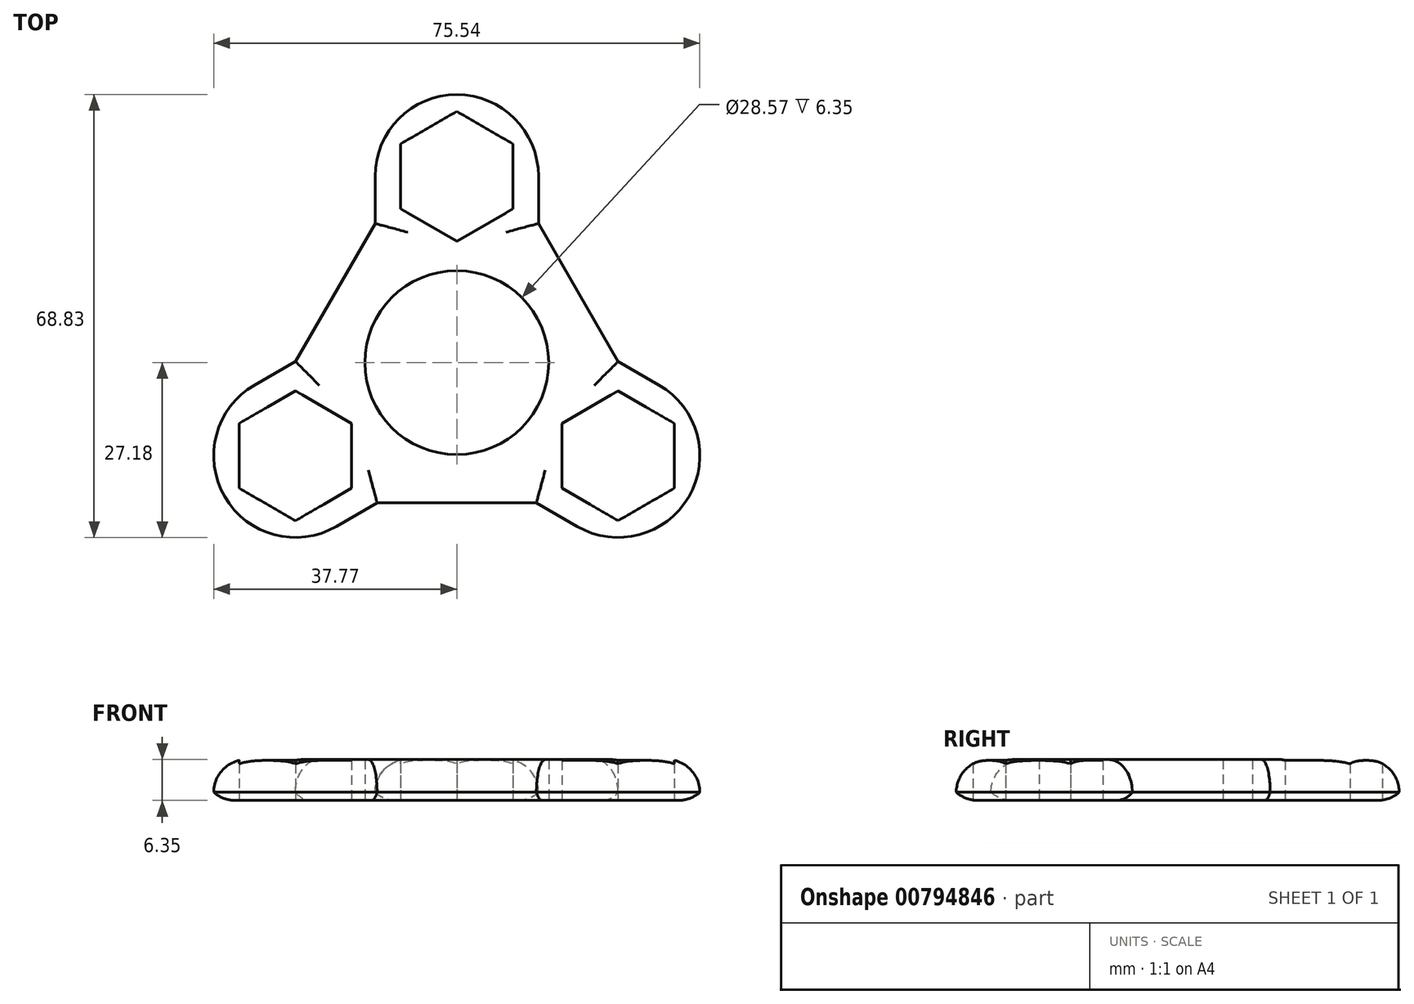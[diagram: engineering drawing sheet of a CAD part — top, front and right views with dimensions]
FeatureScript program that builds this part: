
annotation { "Feature Type Name" : "Feature", "Feature Type Description" : "" }
export const myFeature = defineFeature(function(context is Context, id is Id, definition is map)
    precondition{}
    {
        {
            var Q0;
            Q0=qCreatedBy(makeId("Top.planeOp"),FACE);
            var sketch = newSketch(context, id + "F0", { "sketchPlane" : qUnion([Q0])});
            skCircle(sketch, "E0", {"center": v(0, 0) * mm, "radius": 11.02 * mm});
            skCircle(sketch, "E1", {"center": v(0, 0) * mm, "radius": 14.29 * mm});
            skCircle(sketch, "E2.cCircle", {"center": v(0, 28.95) * mm, "radius": 8.74 * mm, "construction": true});
            skLineSegment(sketch, "E2.0", {"start": v(-8.74, 23.9) * mm, "end": v(-8.74, 34) * mm});
            skLineSegment(sketch, "E2.1", {"start": v(-8.74, 34) * mm, "end": v(0, 39.04) * mm});
            skLineSegment(sketch, "E2.2", {"start": v(0, 39.04) * mm, "end": v(8.74, 34) * mm});
            skLineSegment(sketch, "E2.3", {"start": v(8.74, 34) * mm, "end": v(8.74, 23.9) * mm});
            skLineSegment(sketch, "E2.4", {"start": v(8.74, 23.9) * mm, "end": v(0, 18.86) * mm});
            skLineSegment(sketch, "E2.5", {"start": v(0, 18.86) * mm, "end": v(-8.74, 23.9) * mm});
            skPoint(sketch, "E2.0.midPoint", {"position": v(-8.74, 28.95) * mm});
            skCircle(sketch, "E3.cCircle", {"center": v(0, 28.95) * mm, "radius": 12.7 * mm, "construction": true});
            skLineSegment(sketch, "E3.0", {"start": v(-12.7, 21.62) * mm, "end": v(-12.7, 36.28) * mm});
            skLineSegment(sketch, "E3.1", {"start": v(-12.7, 36.28) * mm, "end": v(0, 43.62) * mm});
            skLineSegment(sketch, "E3.2", {"start": v(0, 43.62) * mm, "end": v(12.7, 36.28) * mm});
            skLineSegment(sketch, "E3.3", {"start": v(12.7, 36.28) * mm, "end": v(12.7, 21.62) * mm});
            skLineSegment(sketch, "E3.4", {"start": v(12.7, 21.62) * mm, "end": v(0, 14.29) * mm});
            skLineSegment(sketch, "E3.5", {"start": v(0, 14.29) * mm, "end": v(-12.7, 21.62) * mm});
            skPoint(sketch, "E3.0.midPoint", {"position": v(-12.7, 28.95) * mm});
            skLineSegment(sketch, "E4.1.0", {"start": v(-25.07, -4.39) * mm, "end": v(-16.34, -9.43) * mm});
            skLineSegment(sketch, "E4.1.1", {"start": v(-33.81, -9.43) * mm, "end": v(-25.07, -4.39) * mm});
            skLineSegment(sketch, "E4.1.2", {"start": v(-16.34, -9.43) * mm, "end": v(-16.34, -19.52) * mm});
            skCircle(sketch, "E4.1.3", {"center": v(-25.07, -14.48) * mm, "radius": 12.7 * mm, "construction": true});
            skLineSegment(sketch, "E4.1.4", {"start": v(-12.37, -7.14) * mm, "end": v(-12.37, -21.8) * mm});
            skLineSegment(sketch, "E4.1.5", {"start": v(-12.37, -21.8) * mm, "end": v(-25.07, -29.14) * mm});
            skLineSegment(sketch, "E4.1.6", {"start": v(-25.07, -29.14) * mm, "end": v(-37.77, -21.8) * mm});
            skLineSegment(sketch, "E4.1.7", {"start": v(-25.07, 0.19) * mm, "end": v(-12.37, -7.14) * mm});
            skLineSegment(sketch, "E4.1.8", {"start": v(-37.77, -21.8) * mm, "end": v(-37.77, -7.14) * mm});
            skPoint(sketch, "E4.1.9", {"position": v(-20.7, -22.04) * mm});
            skLineSegment(sketch, "E4.1.10", {"start": v(-33.81, -19.52) * mm, "end": v(-33.81, -9.43) * mm});
            skPoint(sketch, "E4.1.11", {"position": v(-18.72, -25.47) * mm});
            skCircle(sketch, "E4.1.12", {"center": v(-25.07, -14.48) * mm, "radius": 8.74 * mm, "construction": true});
            skLineSegment(sketch, "E4.1.13", {"start": v(-37.77, -7.14) * mm, "end": v(-25.07, 0.19) * mm});
            skLineSegment(sketch, "E4.1.14", {"start": v(-16.34, -19.52) * mm, "end": v(-25.07, -24.57) * mm});
            skLineSegment(sketch, "E4.1.15", {"start": v(-25.07, -24.57) * mm, "end": v(-33.81, -19.52) * mm});
            skLineSegment(sketch, "E4.2.0", {"start": v(16.34, -19.52) * mm, "end": v(16.34, -9.43) * mm});
            skLineSegment(sketch, "E4.2.1", {"start": v(25.07, -24.57) * mm, "end": v(16.34, -19.52) * mm});
            skLineSegment(sketch, "E4.2.2", {"start": v(16.34, -9.43) * mm, "end": v(25.07, -4.39) * mm});
            skCircle(sketch, "E4.2.3", {"center": v(25.07, -14.48) * mm, "radius": 12.7 * mm, "construction": true});
            skLineSegment(sketch, "E4.2.4", {"start": v(12.37, -7.14) * mm, "end": v(25.07, 0.19) * mm});
            skLineSegment(sketch, "E4.2.5", {"start": v(25.07, 0.19) * mm, "end": v(37.77, -7.14) * mm});
            skLineSegment(sketch, "E4.2.6", {"start": v(37.77, -7.14) * mm, "end": v(37.77, -21.8) * mm});
            skLineSegment(sketch, "E4.2.7", {"start": v(12.37, -21.8) * mm, "end": v(12.37, -7.14) * mm});
            skLineSegment(sketch, "E4.2.8", {"start": v(37.77, -21.8) * mm, "end": v(25.07, -29.14) * mm});
            skPoint(sketch, "E4.2.9", {"position": v(29.44, -6.9) * mm});
            skLineSegment(sketch, "E4.2.10", {"start": v(33.81, -19.52) * mm, "end": v(25.07, -24.57) * mm});
            skPoint(sketch, "E4.2.11", {"position": v(31.42, -3.48) * mm});
            skCircle(sketch, "E4.2.12", {"center": v(25.07, -14.48) * mm, "radius": 8.74 * mm, "construction": true});
            skLineSegment(sketch, "E4.2.13", {"start": v(25.07, -29.14) * mm, "end": v(12.37, -21.8) * mm});
            skLineSegment(sketch, "E4.2.14", {"start": v(25.07, -4.39) * mm, "end": v(33.81, -9.43) * mm});
            skLineSegment(sketch, "E4.2.15", {"start": v(33.81, -9.43) * mm, "end": v(33.81, -19.52) * mm});
            skLineSegment(sketch, "E5", {"start": v(-12.7, 21.62) * mm, "end": v(-25.07, 0.19) * mm});
            skLineSegment(sketch, "E6", {"start": v(12.7, 21.62) * mm, "end": v(25.07, 0.19) * mm});
            skLineSegment(sketch, "E7", {"start": v(-12.37, -21.8) * mm, "end": v(12.37, -21.8) * mm});
            skArc(sketch, "E8", {"start": v(12.7, 28.95) * mm, "mid": v(0, 41.65) * mm, "end": v(-12.7, 28.95) * mm});
            skLineSegment(sketch, "E9", {"start": v(-12.7, 28.95) * mm, "end": v(-12.7, 36.28) * mm});
            skLineSegment(sketch, "E10", {"start": v(-12.7, 28.95) * mm, "end": v(-12.7, 36.28) * mm, "construction": true});
            skLineSegment(sketch, "E11", {"start": v(-12.7, 36.28) * mm, "end": v(0, 43.62) * mm, "construction": true});
            skLineSegment(sketch, "E12", {"start": v(0, 43.62) * mm, "end": v(12.7, 36.28) * mm, "construction": true});
            skLineSegment(sketch, "E13", {"start": v(12.7, 36.28) * mm, "end": v(12.7, 28.95) * mm, "construction": true});
            skSolve(sketch);
        }
        {
            var Q0;
            Q0 = qSketchRegion(id + "F0", true);
            extrude(context, id + "F1", {"entities" : qUnion([Q0]), "depth" : 6.35 * mm, "offsetDistance" : 25.4 * mm});
        }
        {
            var Q0;
            Q0=qCreatedBy(makeId("Top.planeOp"),FACE);
            var sketch = newSketch(context, id + "F2", { "sketchPlane" : qUnion([Q0])});
            skArc(sketch, "E14", {"start": v(12.7, 28.95) * mm, "mid": v(0, 41.65) * mm, "end": v(-12.7, 28.95) * mm});
            skLineSegment(sketch, "E15", {"start": v(-12.7, 28.95) * mm, "end": v(-12.7, 36.28) * mm});
            skLineSegment(sketch, "E16", {"start": v(-12.7, 36.28) * mm, "end": v(0, 43.62) * mm});
            skLineSegment(sketch, "E17", {"start": v(0, 43.62) * mm, "end": v(12.7, 36.28) * mm});
            skLineSegment(sketch, "E18", {"start": v(12.7, 36.28) * mm, "end": v(12.7, 28.95) * mm});
            skSolve(sketch);
        }
        {
            var Q0;
            Q0 = qSketchRegion(id + "F2", true);
            extrude(context, id + "F3", {"entities" : qUnion([Q0]), "operationType" : NewBodyOperationType.REMOVE, "endBound" : BoundingType.THROUGH_ALL, "depth" : 25.4 * mm, "offsetDistance" : 25.4 * mm});
        }
        {
            var Q0;
            Q0=qCreatedBy(makeId("Top.planeOp"),FACE);
            var sketch = newSketch(context, id + "F4", { "sketchPlane" : qUnion([Q0])});
            skArc(sketch, "E19", {"start": v(-31.42, -3.48) * mm, "mid": v(-36.07, -20.83) * mm, "end": v(-18.72, -25.47) * mm});
            skLineSegment(sketch, "E20", {"start": v(-31.42, -3.48) * mm, "end": v(-37.77, -7.14) * mm});
            skLineSegment(sketch, "E21", {"start": v(-37.77, -7.14) * mm, "end": v(-37.78, -21.8) * mm});
            skLineSegment(sketch, "E22", {"start": v(-37.78, -21.8) * mm, "end": v(-25.07, -29.14) * mm});
            skLineSegment(sketch, "E23", {"start": v(-25.07, -29.14) * mm, "end": v(-18.72, -25.47) * mm});
            skSolve(sketch);
        }
        {
            var Q0;
            Q0 = qSketchRegion(id + "F4", true);
            extrude(context, id + "F5", {"entities" : qUnion([Q0]), "operationType" : NewBodyOperationType.REMOVE, "endBound" : BoundingType.THROUGH_ALL, "depth" : 25.4 * mm, "offsetDistance" : 25.4 * mm});
        }
        {
            var Q0;
            Q0=qCreatedBy(makeId("Top.planeOp"),FACE);
            var sketch = newSketch(context, id + "F6", { "sketchPlane" : qUnion([Q0])});
            skArc(sketch, "E24", {"start": v(18.72, -25.47) * mm, "mid": v(36.07, -20.83) * mm, "end": v(31.42, -3.48) * mm});
            skLineSegment(sketch, "E25", {"start": v(31.42, -3.48) * mm, "end": v(37.77, -7.14) * mm});
            skLineSegment(sketch, "E26", {"start": v(37.77, -7.14) * mm, "end": v(37.77, -21.8) * mm});
            skLineSegment(sketch, "E27", {"start": v(37.77, -21.8) * mm, "end": v(25.07, -29.14) * mm});
            skLineSegment(sketch, "E28", {"start": v(25.07, -29.14) * mm, "end": v(18.72, -25.47) * mm});
            skSolve(sketch);
        }
        {
            var Q0;
            Q0 = qSketchRegion(id + "F6", true);
            extrude(context, id + "F7", {"entities" : qUnion([Q0]), "operationType" : NewBodyOperationType.REMOVE, "endBound" : BoundingType.THROUGH_ALL, "depth" : 25.4 * mm, "offsetDistance" : 25.4 * mm});
        }
        {
            var Q0;
            {var subQ0=sQuery(id+"F2.wireOp",EDGE,"E14");var subQ2=makeQuery(id+"F2.imprint","INTERSECT",VERTEX,{"derivedFrom":[subQ0,sQuery(id+"F2.wireOp",EDGE,"E17")]});Q0=makeQuery(id+"F3.boolean.opBoolean","INTERSECT",EDGE,{"derivedFrom":[makeQuery(id+"F1.opExtrude","CAP_FACE",FACE,{"disambiguationData":[OSD([sQuery(id+"F0.wireOp",EDGE,"E1"),sQuery(id+"F0.wireOp",EDGE,"E2.0"),sQuery(id+"F0.wireOp",EDGE,"E2.1"),sQuery(id+"F0.wireOp",EDGE,"E2.2"),sQuery(id+"F0.wireOp",EDGE,"E2.3"),sQuery(id+"F0.wireOp",EDGE,"E2.4"),sQuery(id+"F0.wireOp",EDGE,"E2.5"),sQuery(id+"F0.wireOp",EDGE,"E3.0"),sQuery(id+"F0.wireOp",EDGE,"E3.1"),sQuery(id+"F0.wireOp",EDGE,"E3.3"),sQuery(id+"F0.wireOp",EDGE,"E4.1.0"),sQuery(id+"F0.wireOp",EDGE,"E4.1.1"),sQuery(id+"F0.wireOp",EDGE,"E4.1.2"),sQuery(id+"F0.wireOp",EDGE,"E4.1.5"),sQuery(id+"F0.wireOp",EDGE,"E4.1.6"),sQuery(id+"F0.wireOp",EDGE,"E4.1.8"),sQuery(id+"F0.wireOp",EDGE,"E4.1.10"),sQuery(id+"F0.wireOp",EDGE,"E4.1.13"),sQuery(id+"F0.wireOp",EDGE,"E4.1.14"),sQuery(id+"F0.wireOp",EDGE,"E4.1.15"),sQuery(id+"F0.wireOp",EDGE,"E4.2.0"),sQuery(id+"F0.wireOp",EDGE,"E4.2.1"),sQuery(id+"F0.wireOp",EDGE,"E4.2.2"),sQuery(id+"F0.wireOp",EDGE,"E4.2.5"),sQuery(id+"F0.wireOp",EDGE,"E4.2.6"),sQuery(id+"F0.wireOp",EDGE,"E4.2.8"),sQuery(id+"F0.wireOp",EDGE,"E4.2.10"),sQuery(id+"F0.wireOp",EDGE,"E4.2.13"),sQuery(id+"F0.wireOp",EDGE,"E4.2.14"),sQuery(id+"F0.wireOp",EDGE,"E4.2.15"),sQuery(id+"F0.wireOp",EDGE,"E5"),sQuery(id+"F0.wireOp",EDGE,"E6"),sQuery(id+"F0.wireOp",EDGE,"E7"),sQuery(id+"F0.wireOp",EDGE,"E9"),sQuery(id+"F0.wireOp",EDGE,"E3.2")])],"isStart":false}),makeQuery(id+"F3.opExtrude","SWEPT_FACE",FACE,{"disambiguationData":[OSD([subQ0]),TDD([makeQuery(id+"F2.imprint","IMPRINT",EDGE,{"disambiguationData":[TD([[makeQuery(id+"F2.imprint","INTERSECT",VERTEX,{"derivedFrom":[subQ0,sQuery(id+"F2.wireOp",EDGE,"E18")]}),-1.0]])],"derivedFrom":subQ0})])]}),makeQuery(id+"F3.opExtrude","SWEPT_FACE",FACE,{"disambiguationData":[OSD([subQ0]),TDD([makeQuery(id+"F2.imprint","IMPRINT",EDGE,{"disambiguationData":[TD([[subQ2,-1.0]])],"derivedFrom":subQ0})])]}),makeQuery(id+"F3.opExtrude","SWEPT_FACE",FACE,{"disambiguationData":[OSD([subQ0]),TDD([makeQuery(id+"F2.imprint","IMPRINT",EDGE,{"disambiguationData":[TD([[makeQuery(id+"F2.imprint","INTERSECT",VERTEX,{"derivedFrom":[subQ0,sQuery(id+"F2.wireOp",EDGE,"E15")]}),1.0]])],"derivedFrom":subQ0})])]})]});}
            var Q1;
            Q1=makeQuery(id+"F1.opExtrude","CAP_EDGE",EDGE,{"disambiguationData":[OSD([sQuery(id+"F0.wireOp",EDGE,"E3.3")])],"isStart":false});
            var Q2;
            Q2=makeQuery(id+"F1.opExtrude","CAP_EDGE",EDGE,{"disambiguationData":[OSD([sQuery(id+"F0.wireOp",EDGE,"E6")])],"isStart":false});
            var Q3;
            Q3=makeQuery(id+"F1.opExtrude","CAP_EDGE",EDGE,{"disambiguationData":[OSD([sQuery(id+"F0.wireOp",EDGE,"E4.2.5")])],"isStart":false});
            var Q4;
            {var subQ0=sQuery(id+"F6.wireOp",EDGE,"E24");var subQ2=makeQuery(id+"F6.imprint","INTERSECT",VERTEX,{"derivedFrom":[subQ0,sQuery(id+"F6.wireOp",EDGE,"E27")]});Q4=makeQuery(id+"F7.boolean.opBoolean","INTERSECT",EDGE,{"derivedFrom":[makeQuery(id+"F1.opExtrude","CAP_FACE",FACE,{"disambiguationData":[OSD([sQuery(id+"F0.wireOp",EDGE,"E1"),sQuery(id+"F0.wireOp",EDGE,"E2.0"),sQuery(id+"F0.wireOp",EDGE,"E2.1"),sQuery(id+"F0.wireOp",EDGE,"E2.2"),sQuery(id+"F0.wireOp",EDGE,"E2.3"),sQuery(id+"F0.wireOp",EDGE,"E2.4"),sQuery(id+"F0.wireOp",EDGE,"E2.5"),sQuery(id+"F0.wireOp",EDGE,"E3.0"),sQuery(id+"F0.wireOp",EDGE,"E3.1"),sQuery(id+"F0.wireOp",EDGE,"E3.3"),sQuery(id+"F0.wireOp",EDGE,"E4.1.0"),sQuery(id+"F0.wireOp",EDGE,"E4.1.1"),sQuery(id+"F0.wireOp",EDGE,"E4.1.2"),sQuery(id+"F0.wireOp",EDGE,"E4.1.5"),sQuery(id+"F0.wireOp",EDGE,"E4.1.6"),sQuery(id+"F0.wireOp",EDGE,"E4.1.8"),sQuery(id+"F0.wireOp",EDGE,"E4.1.10"),sQuery(id+"F0.wireOp",EDGE,"E4.1.13"),sQuery(id+"F0.wireOp",EDGE,"E4.1.14"),sQuery(id+"F0.wireOp",EDGE,"E4.1.15"),sQuery(id+"F0.wireOp",EDGE,"E4.2.0"),sQuery(id+"F0.wireOp",EDGE,"E4.2.1"),sQuery(id+"F0.wireOp",EDGE,"E4.2.2"),sQuery(id+"F0.wireOp",EDGE,"E4.2.5"),sQuery(id+"F0.wireOp",EDGE,"E4.2.6"),sQuery(id+"F0.wireOp",EDGE,"E4.2.8"),sQuery(id+"F0.wireOp",EDGE,"E4.2.10"),sQuery(id+"F0.wireOp",EDGE,"E4.2.13"),sQuery(id+"F0.wireOp",EDGE,"E4.2.14"),sQuery(id+"F0.wireOp",EDGE,"E4.2.15"),sQuery(id+"F0.wireOp",EDGE,"E5"),sQuery(id+"F0.wireOp",EDGE,"E6"),sQuery(id+"F0.wireOp",EDGE,"E7"),sQuery(id+"F0.wireOp",EDGE,"E9"),sQuery(id+"F0.wireOp",EDGE,"E3.2")])],"isStart":false}),makeQuery(id+"F7.opExtrude","SWEPT_FACE",FACE,{"disambiguationData":[OSD([subQ0]),TDD([makeQuery(id+"F6.imprint","IMPRINT",EDGE,{"disambiguationData":[TD([[makeQuery(id+"F6.imprint","INTERSECT",VERTEX,{"derivedFrom":[subQ0,sQuery(id+"F6.wireOp",EDGE,"E28")]}),-1.0]])],"derivedFrom":subQ0})])]}),makeQuery(id+"F7.opExtrude","SWEPT_FACE",FACE,{"disambiguationData":[OSD([subQ0]),TDD([makeQuery(id+"F6.imprint","IMPRINT",EDGE,{"disambiguationData":[TD([[subQ2,-1.0]])],"derivedFrom":subQ0})])]}),makeQuery(id+"F7.opExtrude","SWEPT_FACE",FACE,{"disambiguationData":[OSD([subQ0]),TDD([makeQuery(id+"F6.imprint","IMPRINT",EDGE,{"disambiguationData":[TD([[makeQuery(id+"F6.imprint","INTERSECT",VERTEX,{"derivedFrom":[subQ0,sQuery(id+"F6.wireOp",EDGE,"E25")]}),1.0]])],"derivedFrom":subQ0})])]})]});}
            var Q5;
            Q5=makeQuery(id+"F1.opExtrude","CAP_EDGE",EDGE,{"disambiguationData":[OSD([sQuery(id+"F0.wireOp",EDGE,"E4.2.13")])],"isStart":false});
            var Q6;
            Q6=makeQuery(id+"F1.opExtrude","CAP_EDGE",EDGE,{"disambiguationData":[OSD([sQuery(id+"F0.wireOp",EDGE,"E7")])],"isStart":false});
            var Q7;
            Q7=makeQuery(id+"F1.opExtrude","CAP_EDGE",EDGE,{"disambiguationData":[OSD([sQuery(id+"F0.wireOp",EDGE,"E4.1.5")])],"isStart":false});
            var Q8;
            {var subQ0=sQuery(id+"F4.wireOp",EDGE,"E19");var subQ2=makeQuery(id+"F4.imprint","INTERSECT",VERTEX,{"derivedFrom":[subQ0,sQuery(id+"F4.wireOp",EDGE,"E21")]});Q8=makeQuery(id+"F5.boolean.opBoolean","INTERSECT",EDGE,{"derivedFrom":[makeQuery(id+"F1.opExtrude","CAP_FACE",FACE,{"disambiguationData":[OSD([sQuery(id+"F0.wireOp",EDGE,"E1"),sQuery(id+"F0.wireOp",EDGE,"E2.0"),sQuery(id+"F0.wireOp",EDGE,"E2.1"),sQuery(id+"F0.wireOp",EDGE,"E2.2"),sQuery(id+"F0.wireOp",EDGE,"E2.3"),sQuery(id+"F0.wireOp",EDGE,"E2.4"),sQuery(id+"F0.wireOp",EDGE,"E2.5"),sQuery(id+"F0.wireOp",EDGE,"E3.0"),sQuery(id+"F0.wireOp",EDGE,"E3.1"),sQuery(id+"F0.wireOp",EDGE,"E3.3"),sQuery(id+"F0.wireOp",EDGE,"E4.1.0"),sQuery(id+"F0.wireOp",EDGE,"E4.1.1"),sQuery(id+"F0.wireOp",EDGE,"E4.1.2"),sQuery(id+"F0.wireOp",EDGE,"E4.1.5"),sQuery(id+"F0.wireOp",EDGE,"E4.1.6"),sQuery(id+"F0.wireOp",EDGE,"E4.1.8"),sQuery(id+"F0.wireOp",EDGE,"E4.1.10"),sQuery(id+"F0.wireOp",EDGE,"E4.1.13"),sQuery(id+"F0.wireOp",EDGE,"E4.1.14"),sQuery(id+"F0.wireOp",EDGE,"E4.1.15"),sQuery(id+"F0.wireOp",EDGE,"E4.2.0"),sQuery(id+"F0.wireOp",EDGE,"E4.2.1"),sQuery(id+"F0.wireOp",EDGE,"E4.2.2"),sQuery(id+"F0.wireOp",EDGE,"E4.2.5"),sQuery(id+"F0.wireOp",EDGE,"E4.2.6"),sQuery(id+"F0.wireOp",EDGE,"E4.2.8"),sQuery(id+"F0.wireOp",EDGE,"E4.2.10"),sQuery(id+"F0.wireOp",EDGE,"E4.2.13"),sQuery(id+"F0.wireOp",EDGE,"E4.2.14"),sQuery(id+"F0.wireOp",EDGE,"E4.2.15"),sQuery(id+"F0.wireOp",EDGE,"E5"),sQuery(id+"F0.wireOp",EDGE,"E6"),sQuery(id+"F0.wireOp",EDGE,"E7"),sQuery(id+"F0.wireOp",EDGE,"E9"),sQuery(id+"F0.wireOp",EDGE,"E3.2")])],"isStart":false}),makeQuery(id+"F5.opExtrude","SWEPT_FACE",FACE,{"disambiguationData":[OSD([subQ0]),TDD([makeQuery(id+"F4.imprint","IMPRINT",EDGE,{"disambiguationData":[TD([[makeQuery(id+"F4.imprint","INTERSECT",VERTEX,{"derivedFrom":[subQ0,sQuery(id+"F4.wireOp",EDGE,"E20")]}),-1.0]])],"derivedFrom":subQ0})])]}),makeQuery(id+"F5.opExtrude","SWEPT_FACE",FACE,{"disambiguationData":[OSD([subQ0]),TDD([makeQuery(id+"F4.imprint","IMPRINT",EDGE,{"disambiguationData":[TD([[subQ2,-1.0]])],"derivedFrom":subQ0})])]}),makeQuery(id+"F5.opExtrude","SWEPT_FACE",FACE,{"disambiguationData":[OSD([subQ0]),TDD([makeQuery(id+"F4.imprint","IMPRINT",EDGE,{"disambiguationData":[TD([[makeQuery(id+"F4.imprint","INTERSECT",VERTEX,{"derivedFrom":[subQ0,sQuery(id+"F4.wireOp",EDGE,"E23")]}),1.0]])],"derivedFrom":subQ0})])]})]});}
            var Q9;
            Q9=makeQuery(id+"F1.opExtrude","CAP_EDGE",EDGE,{"disambiguationData":[OSD([sQuery(id+"F0.wireOp",EDGE,"E4.1.13")])],"isStart":false});
            var Q10;
            Q10=makeQuery(id+"F1.opExtrude","CAP_EDGE",EDGE,{"disambiguationData":[OSD([sQuery(id+"F0.wireOp",EDGE,"E5")])],"isStart":false});
            var Q11;
            Q11=makeQuery(id+"F1.opExtrude","CAP_EDGE",EDGE,{"disambiguationData":[OSD([sQuery(id+"F0.wireOp",EDGE,"E3.0"),sQuery(id+"F0.wireOp",EDGE,"E9")])],"isStart":false});
            fillet(context, id + "F8", {"entities" : qUnion([Q0, Q1, Q2, Q3, Q4, Q5, Q6, Q7, Q8, Q9, Q10, Q11]), "radius" : 5.08 * mm, "tangentPropagation" : true, "allowEdgeOverflow" : false});
        }
        {
            var Q0;
            {var subQ0=sQuery(id+"F4.wireOp",EDGE,"E19");var subQ2=makeQuery(id+"F4.imprint","INTERSECT",VERTEX,{"derivedFrom":[subQ0,sQuery(id+"F4.wireOp",EDGE,"E21")]});Q0=makeQuery(id+"F5.boolean.opBoolean","TWEAK_EDGE",EDGE,{"derivedFrom":[makeQuery(id+"F5.opExtrude","CAP_EDGE",EDGE,{"disambiguationData":[OSD([subQ0]),TDD([makeQuery(id+"F4.imprint","IMPRINT",EDGE,{"disambiguationData":[TD([[makeQuery(id+"F4.imprint","INTERSECT",VERTEX,{"derivedFrom":[subQ0,sQuery(id+"F4.wireOp",EDGE,"E20")]}),-1.0]])],"derivedFrom":subQ0})])],"isStart":true}),makeQuery(id+"F5.opExtrude","CAP_EDGE",EDGE,{"disambiguationData":[OSD([subQ0]),TDD([makeQuery(id+"F4.imprint","IMPRINT",EDGE,{"disambiguationData":[TD([[subQ2,-1.0]])],"derivedFrom":subQ0})])],"isStart":true}),makeQuery(id+"F5.opExtrude","CAP_EDGE",EDGE,{"disambiguationData":[OSD([subQ0]),TDD([makeQuery(id+"F4.imprint","IMPRINT",EDGE,{"disambiguationData":[TD([[makeQuery(id+"F4.imprint","INTERSECT",VERTEX,{"derivedFrom":[subQ0,sQuery(id+"F4.wireOp",EDGE,"E23")]}),1.0]])],"derivedFrom":subQ0})])],"isStart":true})]});}
            var Q1;
            Q1=makeQuery(id+"F1.opExtrude","CAP_EDGE",EDGE,{"disambiguationData":[OSD([sQuery(id+"F0.wireOp",EDGE,"E4.1.5")])],"isStart":true});
            var Q2;
            Q2=makeQuery(id+"F1.opExtrude","CAP_EDGE",EDGE,{"disambiguationData":[OSD([sQuery(id+"F0.wireOp",EDGE,"E7")])],"isStart":true});
            var Q3;
            Q3=makeQuery(id+"F1.opExtrude","CAP_EDGE",EDGE,{"disambiguationData":[OSD([sQuery(id+"F0.wireOp",EDGE,"E4.2.13")])],"isStart":true});
            var Q4;
            {var subQ0=sQuery(id+"F6.wireOp",EDGE,"E24");var subQ2=makeQuery(id+"F6.imprint","INTERSECT",VERTEX,{"derivedFrom":[subQ0,sQuery(id+"F6.wireOp",EDGE,"E27")]});Q4=makeQuery(id+"F7.boolean.opBoolean","TWEAK_EDGE",EDGE,{"derivedFrom":[makeQuery(id+"F7.opExtrude","CAP_EDGE",EDGE,{"disambiguationData":[OSD([subQ0]),TDD([makeQuery(id+"F6.imprint","IMPRINT",EDGE,{"disambiguationData":[TD([[makeQuery(id+"F6.imprint","INTERSECT",VERTEX,{"derivedFrom":[subQ0,sQuery(id+"F6.wireOp",EDGE,"E28")]}),-1.0]])],"derivedFrom":subQ0})])],"isStart":true}),makeQuery(id+"F7.opExtrude","CAP_EDGE",EDGE,{"disambiguationData":[OSD([subQ0]),TDD([makeQuery(id+"F6.imprint","IMPRINT",EDGE,{"disambiguationData":[TD([[subQ2,-1.0]])],"derivedFrom":subQ0})])],"isStart":true}),makeQuery(id+"F7.opExtrude","CAP_EDGE",EDGE,{"disambiguationData":[OSD([subQ0]),TDD([makeQuery(id+"F6.imprint","IMPRINT",EDGE,{"disambiguationData":[TD([[makeQuery(id+"F6.imprint","INTERSECT",VERTEX,{"derivedFrom":[subQ0,sQuery(id+"F6.wireOp",EDGE,"E25")]}),1.0]])],"derivedFrom":subQ0})])],"isStart":true})]});}
            var Q5;
            Q5=makeQuery(id+"F1.opExtrude","CAP_EDGE",EDGE,{"disambiguationData":[OSD([sQuery(id+"F0.wireOp",EDGE,"E4.2.5")])],"isStart":true});
            var Q6;
            Q6=makeQuery(id+"F1.opExtrude","CAP_EDGE",EDGE,{"disambiguationData":[OSD([sQuery(id+"F0.wireOp",EDGE,"E6")])],"isStart":true});
            var Q7;
            Q7=makeQuery(id+"F1.opExtrude","CAP_EDGE",EDGE,{"disambiguationData":[OSD([sQuery(id+"F0.wireOp",EDGE,"E3.3")])],"isStart":true});
            var Q8;
            {var subQ0=sQuery(id+"F2.wireOp",EDGE,"E14");var subQ2=makeQuery(id+"F2.imprint","INTERSECT",VERTEX,{"derivedFrom":[subQ0,sQuery(id+"F2.wireOp",EDGE,"E17")]});Q8=makeQuery(id+"F3.boolean.opBoolean","TWEAK_EDGE",EDGE,{"derivedFrom":[makeQuery(id+"F3.opExtrude","CAP_EDGE",EDGE,{"disambiguationData":[OSD([subQ0]),TDD([makeQuery(id+"F2.imprint","IMPRINT",EDGE,{"disambiguationData":[TD([[makeQuery(id+"F2.imprint","INTERSECT",VERTEX,{"derivedFrom":[subQ0,sQuery(id+"F2.wireOp",EDGE,"E18")]}),-1.0]])],"derivedFrom":subQ0})])],"isStart":true}),makeQuery(id+"F3.opExtrude","CAP_EDGE",EDGE,{"disambiguationData":[OSD([subQ0]),TDD([makeQuery(id+"F2.imprint","IMPRINT",EDGE,{"disambiguationData":[TD([[subQ2,-1.0]])],"derivedFrom":subQ0})])],"isStart":true}),makeQuery(id+"F3.opExtrude","CAP_EDGE",EDGE,{"disambiguationData":[OSD([subQ0]),TDD([makeQuery(id+"F2.imprint","IMPRINT",EDGE,{"disambiguationData":[TD([[makeQuery(id+"F2.imprint","INTERSECT",VERTEX,{"derivedFrom":[subQ0,sQuery(id+"F2.wireOp",EDGE,"E15")]}),1.0]])],"derivedFrom":subQ0})])],"isStart":true})]});}
            var Q9;
            Q9=makeQuery(id+"F1.opExtrude","CAP_EDGE",EDGE,{"disambiguationData":[OSD([sQuery(id+"F0.wireOp",EDGE,"E3.0"),sQuery(id+"F0.wireOp",EDGE,"E9")])],"isStart":true});
            var Q10;
            Q10=makeQuery(id+"F1.opExtrude","CAP_EDGE",EDGE,{"disambiguationData":[OSD([sQuery(id+"F0.wireOp",EDGE,"E5")])],"isStart":true});
            var Q11;
            Q11=makeQuery(id+"F1.opExtrude","CAP_EDGE",EDGE,{"disambiguationData":[OSD([sQuery(id+"F0.wireOp",EDGE,"E4.1.13")])],"isStart":true});
            fillet(context, id + "F9", {"entities" : qUnion([Q0, Q1, Q2, Q3, Q4, Q5, Q6, Q7, Q8, Q9, Q10, Q11]), "radius" : 5.08 * mm, "tangentPropagation" : true, "allowEdgeOverflow" : false});
        }
    });
